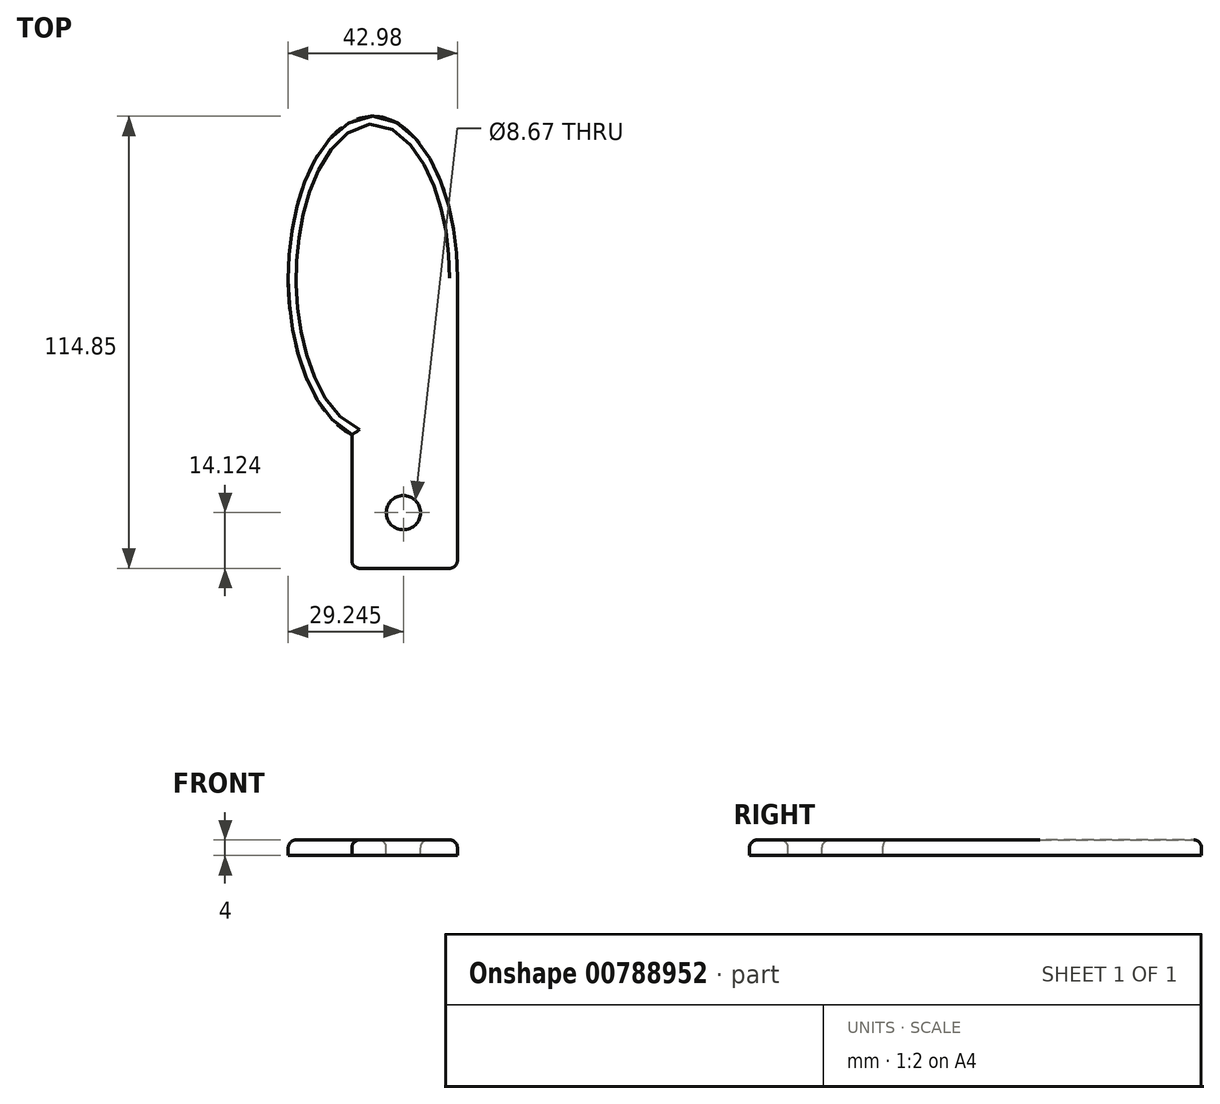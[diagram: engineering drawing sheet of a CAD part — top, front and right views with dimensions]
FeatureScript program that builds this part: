
annotation { "Feature Type Name" : "Feature", "Feature Type Description" : "" }
export const myFeature = defineFeature(function(context is Context, id is Id, definition is map)
    precondition{}
    {
        {
            var Q0;
            Q0=qCreatedBy(makeId("Top.planeOp"),FACE);
            var sketch = newSketch(context, id + "F0", { "sketchPlane" : qUnion([Q0])});
            skEllipse(sketch, "E0", {"center": v(0, 0) * mm, "majorRadius": 41.1 * mm, "minorRadius": 21.5 * mm, "majorAxis": v(0, -1)});
            skLineSegment(sketch, "E1", {"start": v(21.5, 0) * mm, "end": v(21.5, -73.76) * mm});
            skLineSegment(sketch, "E2", {"start": v(21.5, -73.76) * mm, "end": v(-5.33, -73.76) * mm});
            skLineSegment(sketch, "E3", {"start": v(-5.33, -73.76) * mm, "end": v(-5.33, -39.81) * mm});
            skCircle(sketch, "E4", {"center": v(7.75, -59.64) * mm, "radius": 4.34 * mm});
            skSolve(sketch);
        }
        {
            var Q0;
            {var subQ0=sQuery(id+"F0.wireOp",EDGE,"E0");var subQ1=makeQuery(id+"F0.imprint","INTERSECT",VERTEX,{"derivedFrom":[subQ0,sQuery(id+"F0.wireOp",EDGE,"E1")]});Q0=makeQuery(id+"F0.imprint","IMPRINT",FACE,{"disambiguationData":[TD([[makeQuery(id+"F0.imprint","IMPRINT",EDGE,{"disambiguationData":[TD([[subQ1,-1.0]])],"derivedFrom":subQ0}),1.0]])]});}
            var Q1;
            {var subQ1=sQuery(id+"F0.wireOp",EDGE,"E1");Q1=makeQuery(id+"F0.imprint","IMPRINT",FACE,{"disambiguationData":[TD([[makeQuery(id+"F0.imprint","IMPRINT",EDGE,{"derivedFrom":subQ1}),-1.0]])]});}
            extrude(context, id + "F1", {"entities" : qUnion([Q0, Q1]), "oppositeDirection" : true, "depth" : 4 * mm, "offsetDistance" : 25 * mm});
        }
        {
            var Q0;
            {var subQ0=sQuery(id+"F0.wireOp",EDGE,"E2");var subQ1=sQuery(id+"F0.wireOp",EDGE,"E1");var subQ2=sQuery(id+"F0.wireOp",EDGE,"E3");var subQ3=sQuery(id+"F0.wireOp",EDGE,"E0");var subQ4=sQuery(id+"F0.wireOp",EDGE,"WRFZsre6-WHjS-VLdj-HqVo-3cEF5hGJTSZk");Q0=makeQuery(id+"FBbu4MpCb8E052E_1.boolean.opBoolean","SPLIT",FACE,{"disambiguationData":[TD([makeQuery(id+"F1.opExtrude","SWEPT_FACE",FACE,{"disambiguationData":[OSD([subQ3])]})])],"derivedFrom":makeQuery(id+"F1.opExtrude","CAP_FACE",FACE,{"disambiguationData":[OSD([subQ3,subQ1,subQ0,subQ2,subQ4])],"isStart":true})});}
            fillet(context, id + "F2", {"entities" : qUnion([Q0]), "radius" : 2 * mm, "tangentPropagation" : true, "allowEdgeOverflow" : false});
        }
        {
            var Q0;
            Q0=makeQuery(id+"F1.opExtrude","SWEPT_EDGE",EDGE,{"disambiguationData":[OSD([sQuery(id+"F0.wireOp",EDGE,"E1"),sQuery(id+"F0.wireOp",EDGE,"E2")])]});
            var Q1;
            Q1=makeQuery(id+"F1.opExtrude","SWEPT_EDGE",EDGE,{"disambiguationData":[OSD([sQuery(id+"F0.wireOp",EDGE,"E2"),sQuery(id+"F0.wireOp",EDGE,"E3")])]});
            fillet(context, id + "F3", {"entities" : qUnion([Q0, Q1]), "radius" : 2 * mm, "tangentPropagation" : true, "allowEdgeOverflow" : false});
        }
    });
